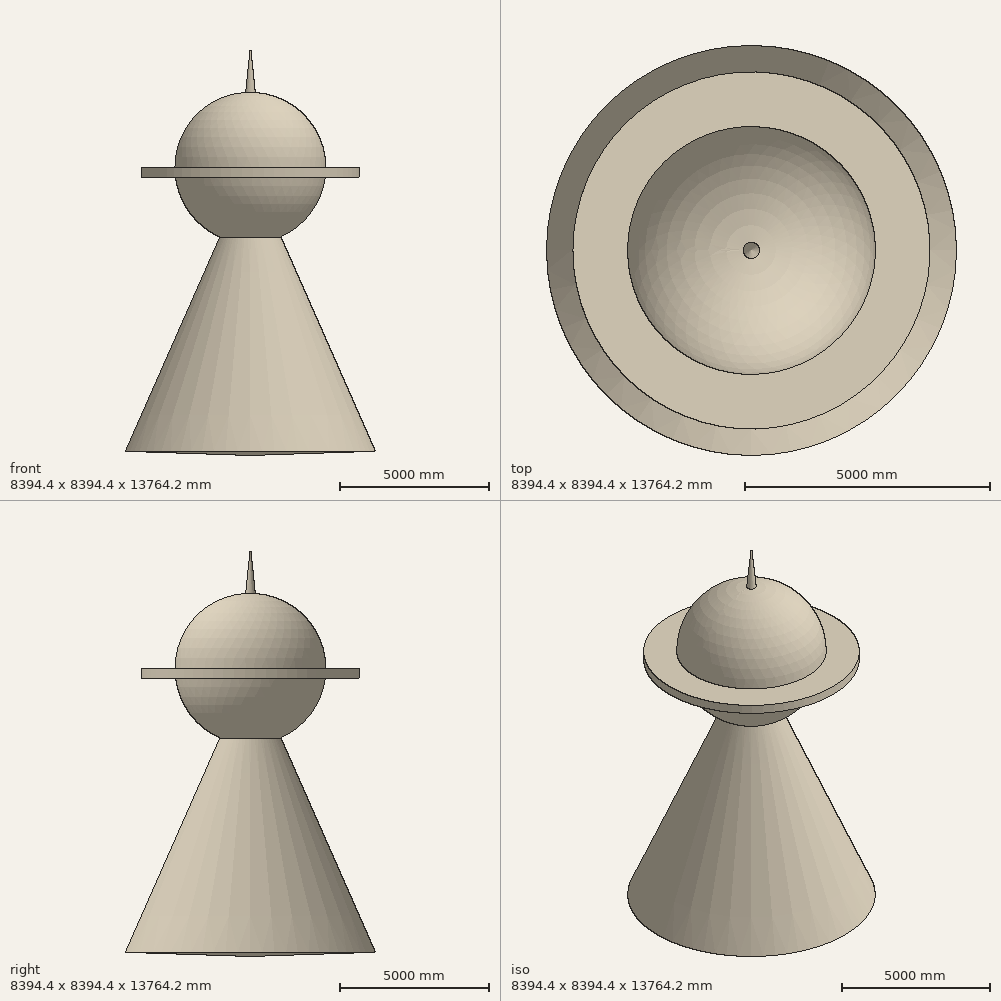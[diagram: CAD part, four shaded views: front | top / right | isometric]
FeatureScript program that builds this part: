
annotation { "Feature Type Name" : "Feature", "Feature Type Description" : "" }
export const myFeature = defineFeature(function(context is Context, id is Id, definition is map)
    precondition{}
    {
        {
            var Q0;
            Q0=qCreatedBy(makeId("Front.planeOp"),FACE);
            var sketch = newSketch(context, id + "F0", { "sketchPlane" : qUnion([Q0])});
            skLineSegment(sketch, "E0", {"start": v(0, 0) * mm, "end": v(0, 12192) * mm});
            skArc(sketch, "E1", {"start": v(0, 7118.39) * mm, "mid": v(2536.8, 9655.2) * mm, "end": v(0, 12192) * mm});
            skLineSegment(sketch, "E2", {"start": v(0, 0) * mm, "end": v(4197.22, 141.78) * mm});
            skLineSegment(sketch, "E3", {"start": v(4197.22, 141.78) * mm, "end": v(0, 9655.2) * mm});
            skLineSegment(sketch, "E4", {"start": v(2536.8, 9655.2) * mm, "end": v(3655.94, 9655.2) * mm});
            skPoint(sketch, "E4.endSnap0", {"position": v(2536.8, 9655.2) * mm});
            skLineSegment(sketch, "E5", {"start": v(3655.94, 9655.2) * mm, "end": v(3655.94, 9343.55) * mm});
            skLineSegment(sketch, "E6", {"start": v(3655.94, 9343.55) * mm, "end": v(2517.6, 9343.55) * mm});
            skLineSegment(sketch, "E7", {"start": v(0, 12192) * mm, "end": v(0, 13764.19) * mm});
            skLineSegment(sketch, "E8", {"start": v(0, 13764.19) * mm, "end": v(162.66, 12186.78) * mm});
            skSolve(sketch);
        }
        {
            var Q0;
            Q0 = qSketchRegion(id + "F0", true);
            var Q1;
            Q1=sQuery(id+"F0.wireOp",EDGE,"E0");
            revolve(context, id + "F1", {"entities" : qUnion([Q0]), "axis" : qUnion([Q1]), "revolveType" : RevolveType.FULL});
        }
    });
